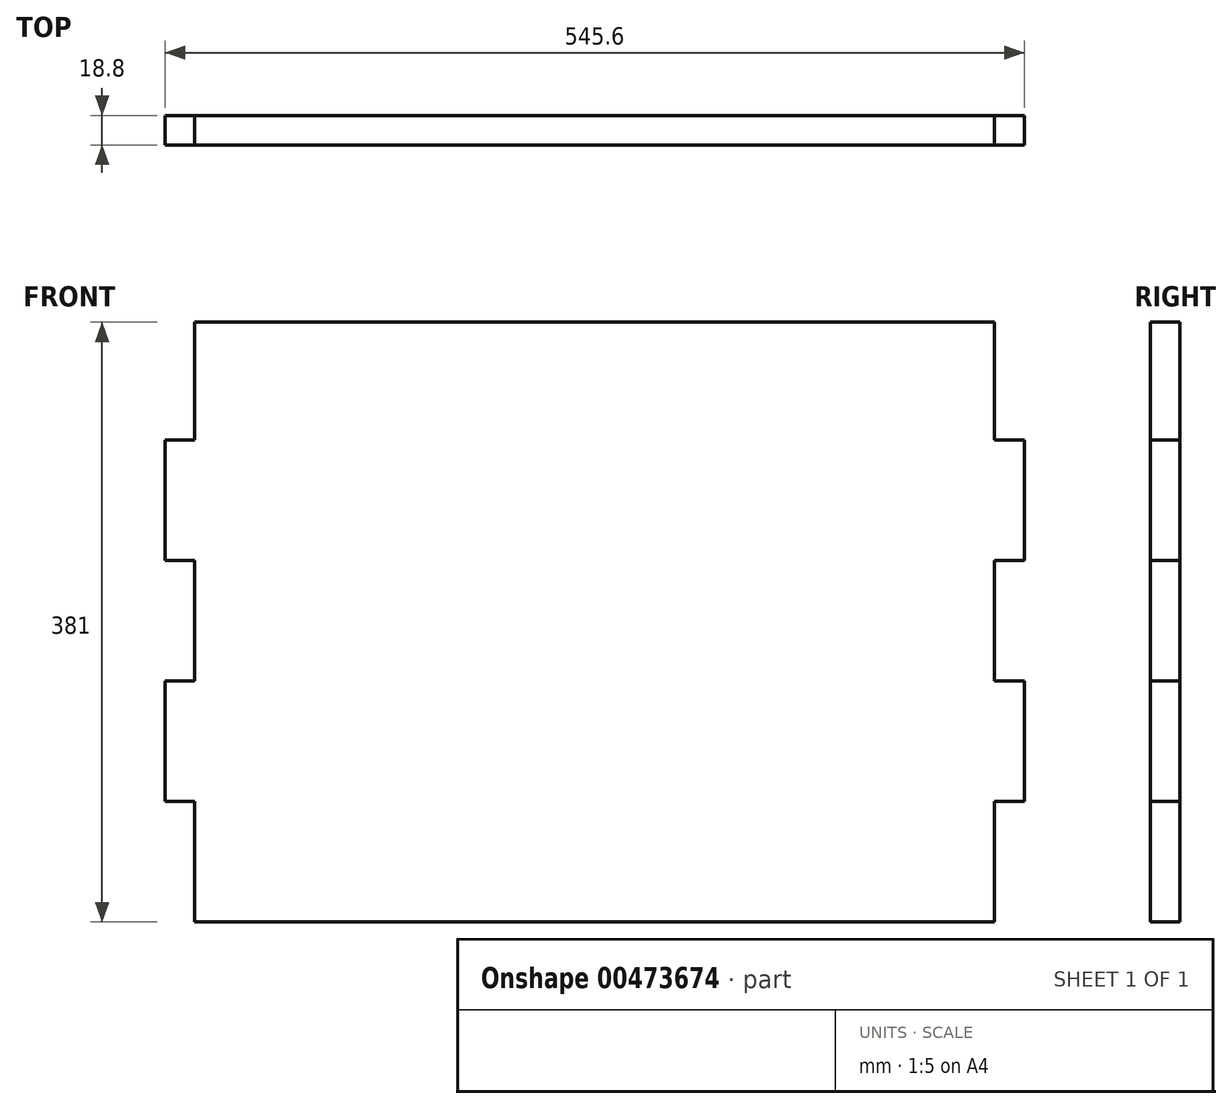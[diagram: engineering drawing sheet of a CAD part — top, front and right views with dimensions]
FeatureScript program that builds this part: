
annotation { "Feature Type Name" : "Feature", "Feature Type Description" : "" }
export const myFeature = defineFeature(function(context is Context, id is Id, definition is map)
    precondition{}
    {
        {
            var Q0;
            Q0=qCreatedBy(makeId("Front.planeOp"),FACE);
            var sketch = newSketch(context, id + "F0", { "sketchPlane" : qUnion([Q0])});
            skLineSegment(sketch, "E0.bottom", {"start": v(254, -191.92) * mm, "end": v(-254, -191.92) * mm});
            skLineSegment(sketch, "E0.top", {"start": v(254, 189.08) * mm, "end": v(-254, 189.08) * mm});
            skPoint(sketch, "E0.middle", {"position": v(0, -1.42) * mm});
            skLineSegment(sketch, "E1", {"start": v(0, 189.08) * mm, "end": v(0, -191.92) * mm});
            skLineSegment(sketch, "E2", {"start": v(-254, -191.92) * mm, "end": v(-254, -115.35) * mm});
            skLineSegment(sketch, "E3", {"start": v(-254, -115.35) * mm, "end": v(-272.8, -115.35) * mm});
            skLineSegment(sketch, "E4", {"start": v(-272.8, -115.35) * mm, "end": v(-272.8, -38.78) * mm});
            skLineSegment(sketch, "E5", {"start": v(-272.8, -38.78) * mm, "end": v(-254, -38.78) * mm});
            skLineSegment(sketch, "E6", {"start": v(-254, -38.78) * mm, "end": v(-254, 37.8) * mm});
            skLineSegment(sketch, "E7", {"start": v(-254, 37.8) * mm, "end": v(-272.8, 37.8) * mm});
            skLineSegment(sketch, "E8", {"start": v(-272.8, 37.8) * mm, "end": v(-272.8, 114.36) * mm});
            skLineSegment(sketch, "E9", {"start": v(-272.8, 114.36) * mm, "end": v(-254, 114.36) * mm});
            skLineSegment(sketch, "E10", {"start": v(-254, 114.36) * mm, "end": v(-254, 189.08) * mm});
            skLineSegment(sketch, "E11.MirrorCS", {"start": v(254, 114.36) * mm, "end": v(254, 189.08) * mm});
            skLineSegment(sketch, "E12.MirrorCS", {"start": v(272.8, 114.36) * mm, "end": v(254, 114.36) * mm});
            skLineSegment(sketch, "E13.MirrorCS", {"start": v(272.8, 37.8) * mm, "end": v(272.8, 114.36) * mm});
            skLineSegment(sketch, "E14.MirrorCS", {"start": v(254, 37.8) * mm, "end": v(272.8, 37.8) * mm});
            skLineSegment(sketch, "E15.MirrorCS", {"start": v(254, -38.78) * mm, "end": v(254, 37.8) * mm});
            skLineSegment(sketch, "E16.MirrorCS", {"start": v(272.8, -38.78) * mm, "end": v(254, -38.78) * mm});
            skLineSegment(sketch, "E17.MirrorCS", {"start": v(272.8, -115.35) * mm, "end": v(272.8, -38.78) * mm});
            skLineSegment(sketch, "E18.MirrorCS", {"start": v(254, -115.35) * mm, "end": v(272.8, -115.35) * mm});
            skLineSegment(sketch, "E19.MirrorCS", {"start": v(254, -191.92) * mm, "end": v(254, -115.35) * mm});
            skSolve(sketch);
        }
        {
            var Q0;
            Q0 = qSketchRegion(id + "F0", true);
            extrude(context, id + "F1", {"entities" : qUnion([Q0]), "depth" : 18.8 * mm, "offsetDistance" : 25.4 * mm});
        }
    });
